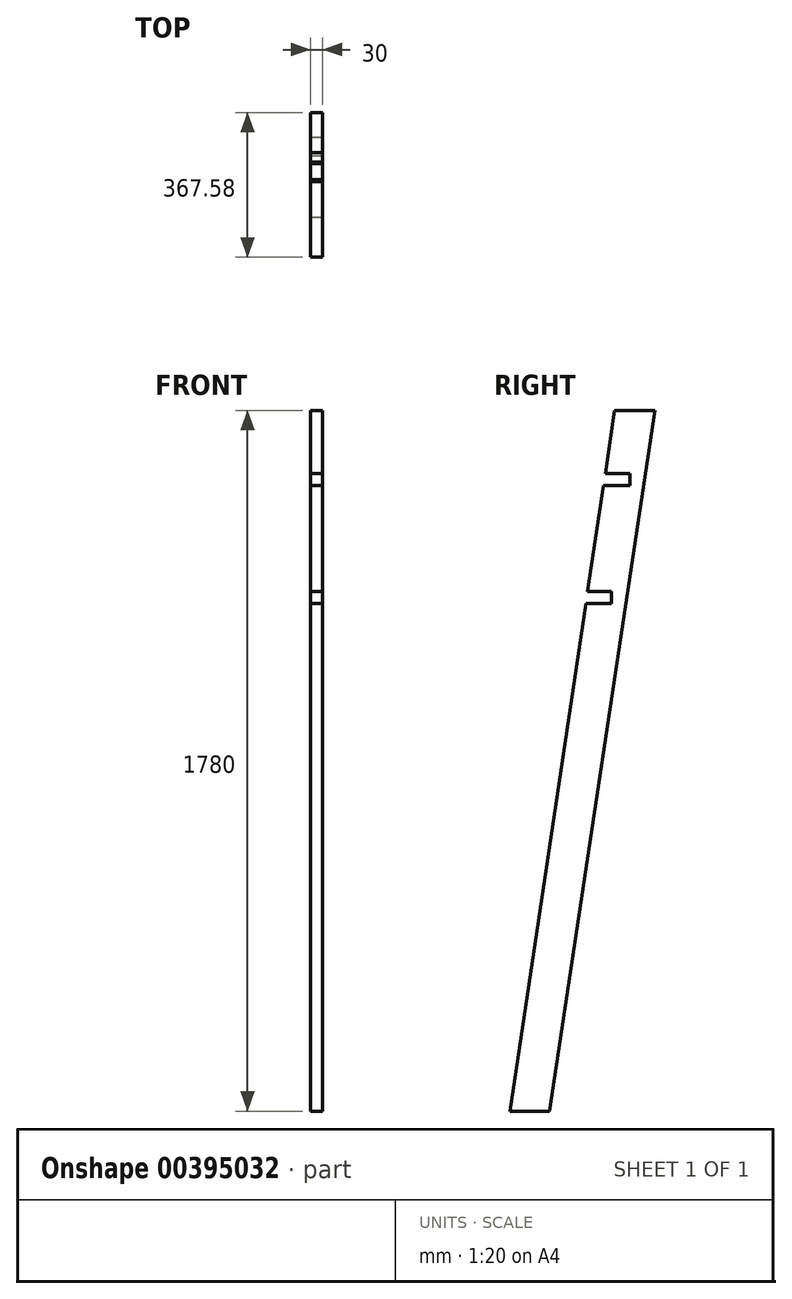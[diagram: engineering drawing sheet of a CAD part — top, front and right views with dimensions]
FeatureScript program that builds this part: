
annotation { "Feature Type Name" : "Feature", "Feature Type Description" : "" }
export const myFeature = defineFeature(function(context is Context, id is Id, definition is map)
    precondition{}
    {
        {
            var Q0;
            Q0=qCreatedBy(makeId("Right.planeOp"),FACE);
            var sketch = newSketch(context, id + "F0", { "sketchPlane" : qUnion([Q0])});
            skLineSegment(sketch, "E0", {"start": v(31.58, 890) * mm, "end": v(133.8, 890) * mm});
            skLineSegment(sketch, "E1", {"start": v(133.8, 890) * mm, "end": v(-133.8, -890) * mm});
            skLineSegment(sketch, "E2", {"start": v(-133.8, -890) * mm, "end": v(-233.8, -890) * mm});
            skLineSegment(sketch, "E3", {"start": v(-233.8, -890) * mm, "end": v(31.58, 890) * mm});
            skSolve(sketch);
        }
        {
            var Q0;
            Q0 = qSketchRegion(id + "F0", true);
            extrude(context, id + "F1", {"entities" : qUnion([Q0]), "depth" : 30 * mm});
        }
        {
            var Q0;
            Q0=qCreatedBy(makeId("Right.planeOp"),FACE);
            var sketch = newSketch(context, id + "F2", { "sketchPlane" : qUnion([Q0])});
            skLineSegment(sketch, "E4.bottom", {"start": v(0, 730) * mm, "end": v(70, 730) * mm});
            skLineSegment(sketch, "E4.top", {"start": v(0, 700) * mm, "end": v(70, 700) * mm});
            skLineSegment(sketch, "E4.left", {"start": v(0, 730) * mm, "end": v(0, 700) * mm});
            skLineSegment(sketch, "E4.right", {"start": v(70, 730) * mm, "end": v(70, 700) * mm});
            skSolve(sketch);
        }
        {
            var Q0;
            Q0 = qSketchRegion(id + "F2", true);
            extrude(context, id + "F3", {"entities" : qUnion([Q0]), "operationType" : NewBodyOperationType.REMOVE, "depth" : 30 * mm});
        }
        {
            var Q0;
            Q0=qCreatedBy(makeId("Right.planeOp"),FACE);
            var sketch = newSketch(context, id + "F4", { "sketchPlane" : qUnion([Q0])});
            skLineSegment(sketch, "E5.bottom", {"start": v(-71.73, 430) * mm, "end": v(23.35, 430) * mm});
            skLineSegment(sketch, "E5.top", {"start": v(-71.73, 400) * mm, "end": v(23.35, 400) * mm});
            skLineSegment(sketch, "E5.left", {"start": v(-71.73, 430) * mm, "end": v(-71.73, 400) * mm});
            skLineSegment(sketch, "E5.right", {"start": v(23.35, 430) * mm, "end": v(23.35, 400) * mm});
            skSolve(sketch);
        }
        {
            var Q0;
            Q0 = qSketchRegion(id + "F4", true);
            extrude(context, id + "F5", {"entities" : qUnion([Q0]), "operationType" : NewBodyOperationType.REMOVE, "depth" : 30 * mm});
        }
    });
